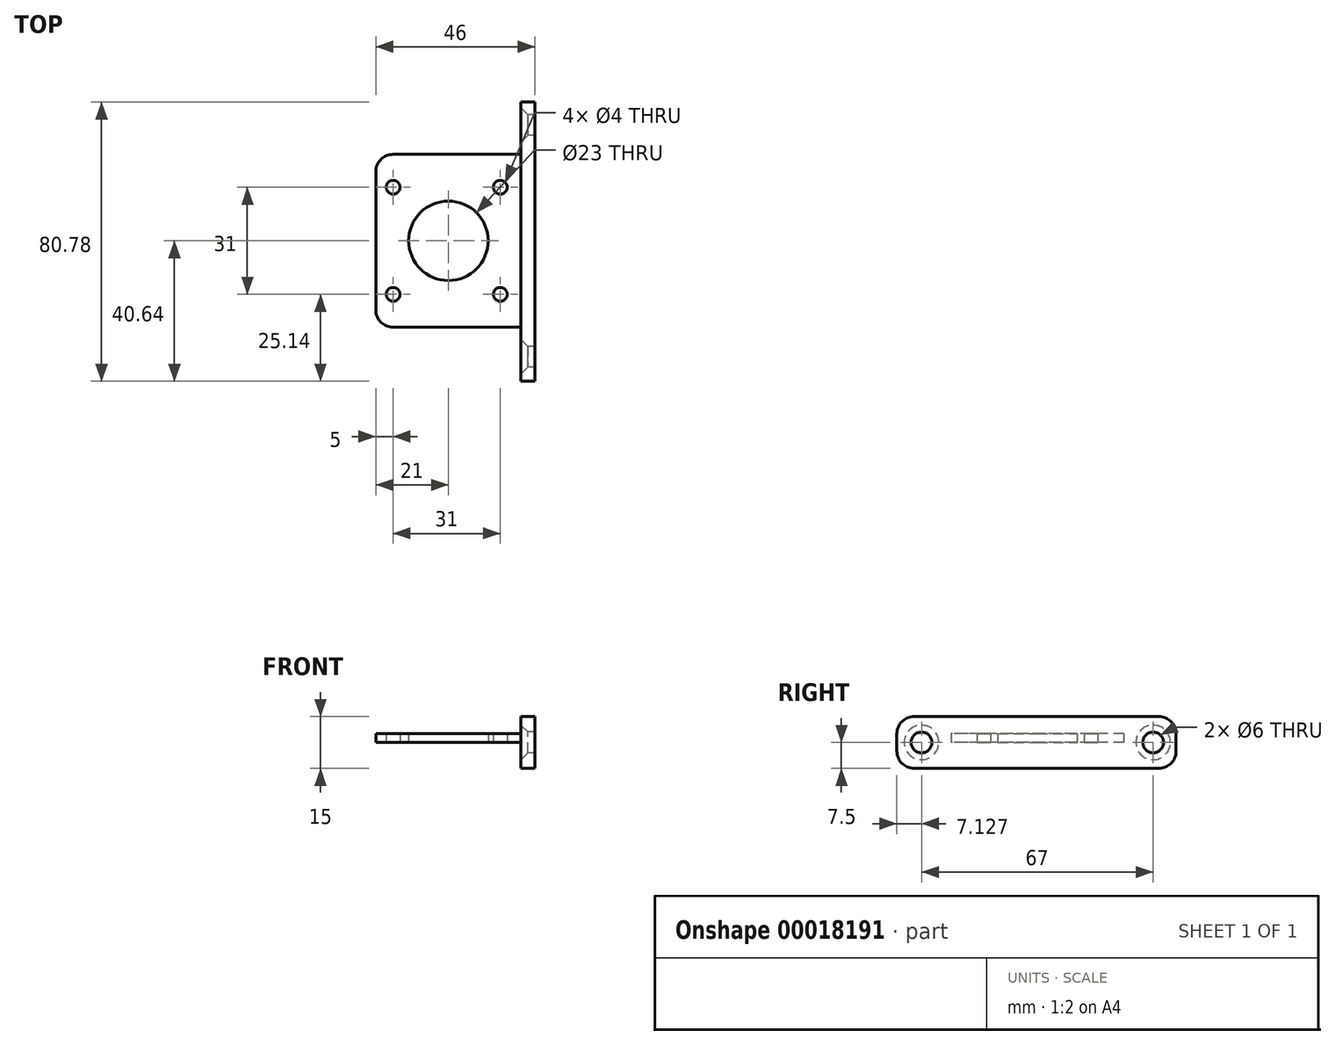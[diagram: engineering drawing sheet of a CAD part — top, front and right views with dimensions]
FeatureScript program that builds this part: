
annotation { "Feature Type Name" : "Feature", "Feature Type Description" : "" }
export const myFeature = defineFeature(function(context is Context, id is Id, definition is map)
    precondition{}
    {
        {
            var Q0;
            Q0=qCreatedBy(makeId("Top.planeOp"),FACE);
            var sketch = newSketch(context, id + "F0", { "sketchPlane" : qUnion([Q0])});
            skLineSegment(sketch, "E0.rect.bottom", {"start": v(-21, 25) * mm, "end": v(21, 25) * mm});
            skLineSegment(sketch, "E0.rect.top", {"start": v(-21, -25) * mm, "end": v(21, -25) * mm});
            skLineSegment(sketch, "E0.rect.left", {"start": v(-21, 25) * mm, "end": v(-21, -25) * mm});
            skLineSegment(sketch, "E0.rect.right", {"start": v(21, 25) * mm, "end": v(21, -25) * mm});
            skPoint(sketch, "E0.rect.middle", {"position": v(0, 0) * mm});
            skLineSegment(sketch, "E1", {"start": v(-21, 15.5) * mm, "end": v(21, 15.5) * mm, "construction": true});
            skLineSegment(sketch, "E2", {"start": v(21, -15.5) * mm, "end": v(-21, -15.5) * mm, "construction": true});
            skLineSegment(sketch, "E3", {"start": v(-16, -25) * mm, "end": v(-16, 25) * mm, "construction": true});
            skLineSegment(sketch, "E4", {"start": v(15, -25) * mm, "end": v(15, 25) * mm, "construction": true});
            skCircle(sketch, "E5", {"center": v(-16, 15.5) * mm, "radius": 2 * mm});
            skCircle(sketch, "E6", {"center": v(15, 15.5) * mm, "radius": 2 * mm});
            skCircle(sketch, "E7", {"center": v(-16, -15.5) * mm, "radius": 2 * mm});
            skCircle(sketch, "E8", {"center": v(15, -15.5) * mm, "radius": 2 * mm});
            skLineSegment(sketch, "E9", {"start": v(-21, 0) * mm, "end": v(21, 0) * mm, "construction": true});
            skCircle(sketch, "E10", {"center": v(0, 0) * mm, "radius": 11.5 * mm});
            skSolve(sketch);
        }
        {
            var Q0;
            Q0 = qSketchRegion(id + "F0", true);
            var Q1;
            Q1=makeQuery(id+"F0.imprint","IMPRINT",FACE,{"disambiguationData":[TD([[makeQuery(id+"F0.imprint","IMPRINT",EDGE,{"derivedFrom":sQuery(id+"F0.wireOp",EDGE,"E0.rect.bottom")}),-1.0]])]});
            extrude(context, id + "F1", {"entities" : qUnion([Q0, Q1]), "depth" : 2.5 * mm});
        }
        {
            var Q0;
            Q0=makeQuery(id+"F1.opExtrude","SWEPT_FACE",FACE,{"disambiguationData":[OSD([sQuery(id+"F0.wireOp",EDGE,"E0.rect.right")])]});
            var sketch = newSketch(context, id + "F2", { "sketchPlane" : qUnion([Q0])});
            skLineSegment(sketch, "E11.bottom", {"start": v(-40.64, 7.5) * mm, "end": v(40.14, 7.5) * mm});
            skLineSegment(sketch, "E11.top", {"start": v(-40.64, -7.5) * mm, "end": v(40.14, -7.5) * mm});
            skLineSegment(sketch, "E11.left", {"start": v(-40.64, 7.5) * mm, "end": v(-40.64, -7.5) * mm});
            skLineSegment(sketch, "E11.right", {"start": v(40.14, 7.5) * mm, "end": v(40.14, -7.5) * mm});
            skLineSegment(sketch, "E12", {"start": v(-40.64, 0) * mm, "end": v(40.14, 0) * mm, "construction": true});
            skCircle(sketch, "E13", {"center": v(-33.51, 0) * mm, "radius": 3 * mm});
            skCircle(sketch, "E14", {"center": v(33.49, 0) * mm, "radius": 3 * mm});
            skSolve(sketch);
        }
        {
            var Q0;
            Q0 = qSketchRegion(id + "F2", true);
            extrude(context, id + "F3", {"entities" : qUnion([Q0]), "operationType" : NewBodyOperationType.ADD, "depth" : 4 * mm});
        }
        {
            var Q0;
            Q0=makeQuery(id+"F3.opExtrude","SWEPT_EDGE",EDGE,{"disambiguationData":[OSD([sQuery(id+"F2.wireOp",EDGE,"E11.bottom"),sQuery(id+"F2.wireOp",EDGE,"E11.left")])]});
            var Q1;
            Q1=makeQuery(id+"F3.opExtrude","SWEPT_EDGE",EDGE,{"disambiguationData":[OSD([sQuery(id+"F2.wireOp",EDGE,"E11.top"),sQuery(id+"F2.wireOp",EDGE,"E11.left")])]});
            var Q2;
            Q2=makeQuery(id+"F3.opExtrude","SWEPT_EDGE",EDGE,{"disambiguationData":[OSD([sQuery(id+"F2.wireOp",EDGE,"E11.bottom"),sQuery(id+"F2.wireOp",EDGE,"E11.right")])]});
            var Q3;
            Q3=makeQuery(id+"F3.opExtrude","SWEPT_EDGE",EDGE,{"disambiguationData":[OSD([sQuery(id+"F2.wireOp",EDGE,"E11.top"),sQuery(id+"F2.wireOp",EDGE,"E11.right")])]});
            fillet(context, id + "F4", {"entities" : qUnion([Q0, Q1, Q2, Q3]), "radius" : 5 * mm, "tangentPropagation" : true, "allowEdgeOverflow" : false});
        }
        {
            var Q0;
            Q0=makeQuery(id+"F1.opExtrude","SWEPT_EDGE",EDGE,{"disambiguationData":[OSD([sQuery(id+"F0.wireOp",EDGE,"E0.rect.top"),sQuery(id+"F0.wireOp",EDGE,"E0.rect.left")])]});
            var Q1;
            Q1=makeQuery(id+"F1.opExtrude","SWEPT_EDGE",EDGE,{"disambiguationData":[OSD([sQuery(id+"F0.wireOp",EDGE,"E0.rect.bottom"),sQuery(id+"F0.wireOp",EDGE,"E0.rect.left")])]});
            fillet(context, id + "F5", {"entities" : qUnion([Q0, Q1]), "radius" : 5 * mm, "tangentPropagation" : true, "allowEdgeOverflow" : false});
        }
        {
            var Q0;
            Q0=makeQuery(id+"F3.opExtrude","CAP_EDGE",EDGE,{"disambiguationData":[OSD([sQuery(id+"F2.wireOp",EDGE,"E14")])],"isStart":true});
            var Q1;
            Q1=makeQuery(id+"F3.opExtrude","CAP_EDGE",EDGE,{"disambiguationData":[OSD([sQuery(id+"F2.wireOp",EDGE,"E13")])],"isStart":true});
            chamfer(context, id + "F6", {"entities" : qUnion([Q0, Q1]), "width" : 2 * mm, "tangentPropagation" : true});
        }
    });
